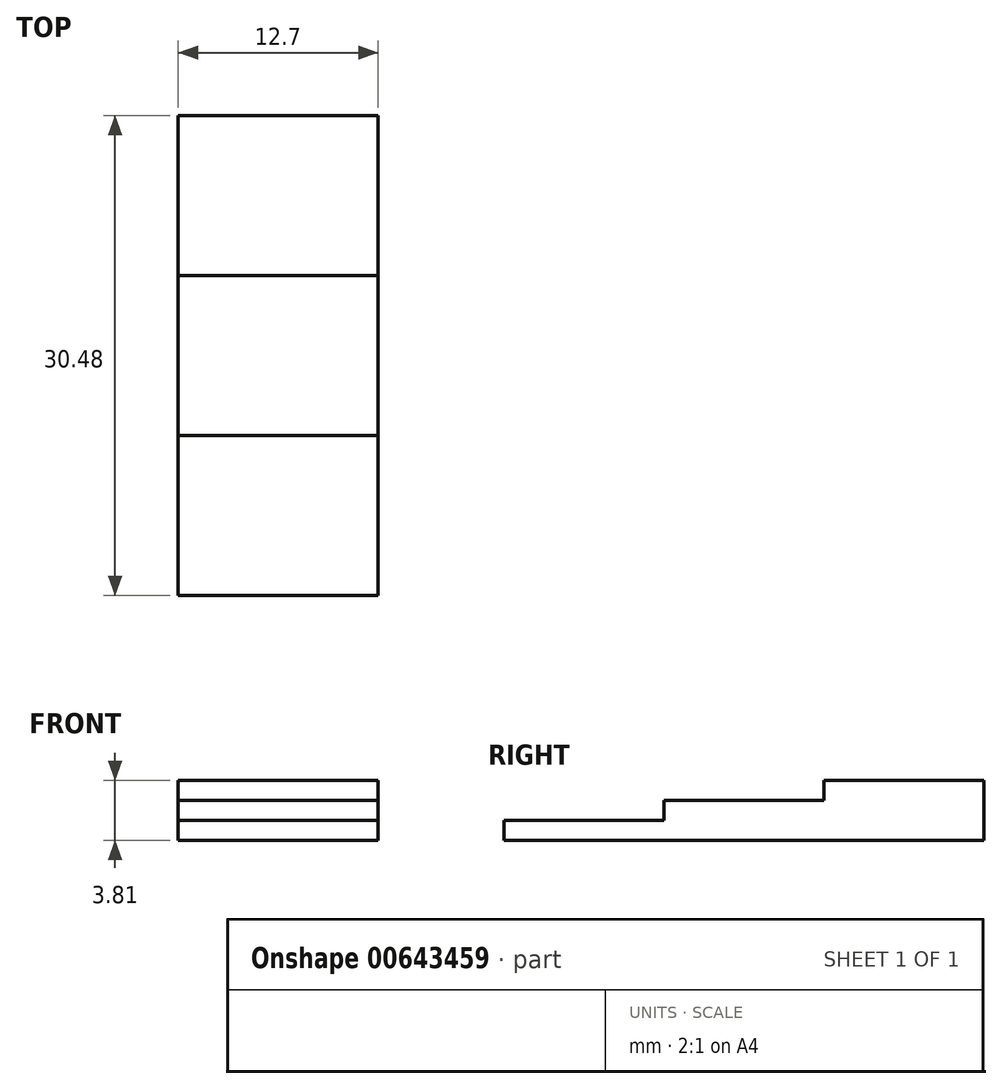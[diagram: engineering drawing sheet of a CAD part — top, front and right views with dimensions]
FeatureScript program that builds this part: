
annotation { "Feature Type Name" : "Feature", "Feature Type Description" : "" }
export const myFeature = defineFeature(function(context is Context, id is Id, definition is map)
    precondition{}
    {
        {
            var Q0;
            Q0=qCreatedBy(makeId("Top.planeOp"),FACE);
            var sketch = newSketch(context, id + "F0", { "sketchPlane" : qUnion([Q0])});
            skLineSegment(sketch, "E0.bottom", {"start": v(0, 0) * mm, "end": v(12.7, 0) * mm});
            skLineSegment(sketch, "E0.top", {"start": v(0, 30.48) * mm, "end": v(12.7, 30.48) * mm});
            skLineSegment(sketch, "E0.left", {"start": v(0, 0) * mm, "end": v(0, 30.48) * mm});
            skLineSegment(sketch, "E0.right", {"start": v(12.7, 0) * mm, "end": v(12.7, 30.48) * mm});
            skLineSegment(sketch, "E1", {"start": v(0, 10.16) * mm, "end": v(12.7, 10.16) * mm});
            skLineSegment(sketch, "E2", {"start": v(0, 20.32) * mm, "end": v(12.7, 20.32) * mm});
            skSolve(sketch);
        }
        {
            var Q0;
            {var subQ0=sQuery(id+"F0.wireOp",EDGE,"E0.bottom");Q0=makeQuery(id+"F0.imprint","IMPRINT",FACE,{"disambiguationData":[TD([[makeQuery(id+"F0.imprint","IMPRINT",EDGE,{"derivedFrom":subQ0}),1.0]])]});}
            extrude(context, id + "F1", {"entities" : qUnion([Q0]), "depth" : 1.27 * mm, "offsetDistance" : 25.4 * mm});
        }
        {
            var Q0;
            {var subQ0=sQuery(id+"F0.wireOp",EDGE,"E1");Q0=makeQuery(id+"F0.imprint","IMPRINT",FACE,{"disambiguationData":[TD([[makeQuery(id+"F0.imprint","IMPRINT",EDGE,{"derivedFrom":subQ0}),1.0]])]});}
            extrude(context, id + "F2", {"entities" : qUnion([Q0]), "operationType" : NewBodyOperationType.ADD, "depth" : 2.54 * mm, "offsetDistance" : 25.4 * mm});
        }
        {
            var Q0;
            {var subQ0=sQuery(id+"F0.wireOp",EDGE,"E0.top");Q0=makeQuery(id+"F0.imprint","IMPRINT",FACE,{"disambiguationData":[TD([[makeQuery(id+"F0.imprint","IMPRINT",EDGE,{"derivedFrom":subQ0}),-1.0]])]});}
            extrude(context, id + "F3", {"entities" : qUnion([Q0]), "operationType" : NewBodyOperationType.ADD, "depth" : 3.8 * mm, "offsetDistance" : 25.4 * mm});
        }
    });
